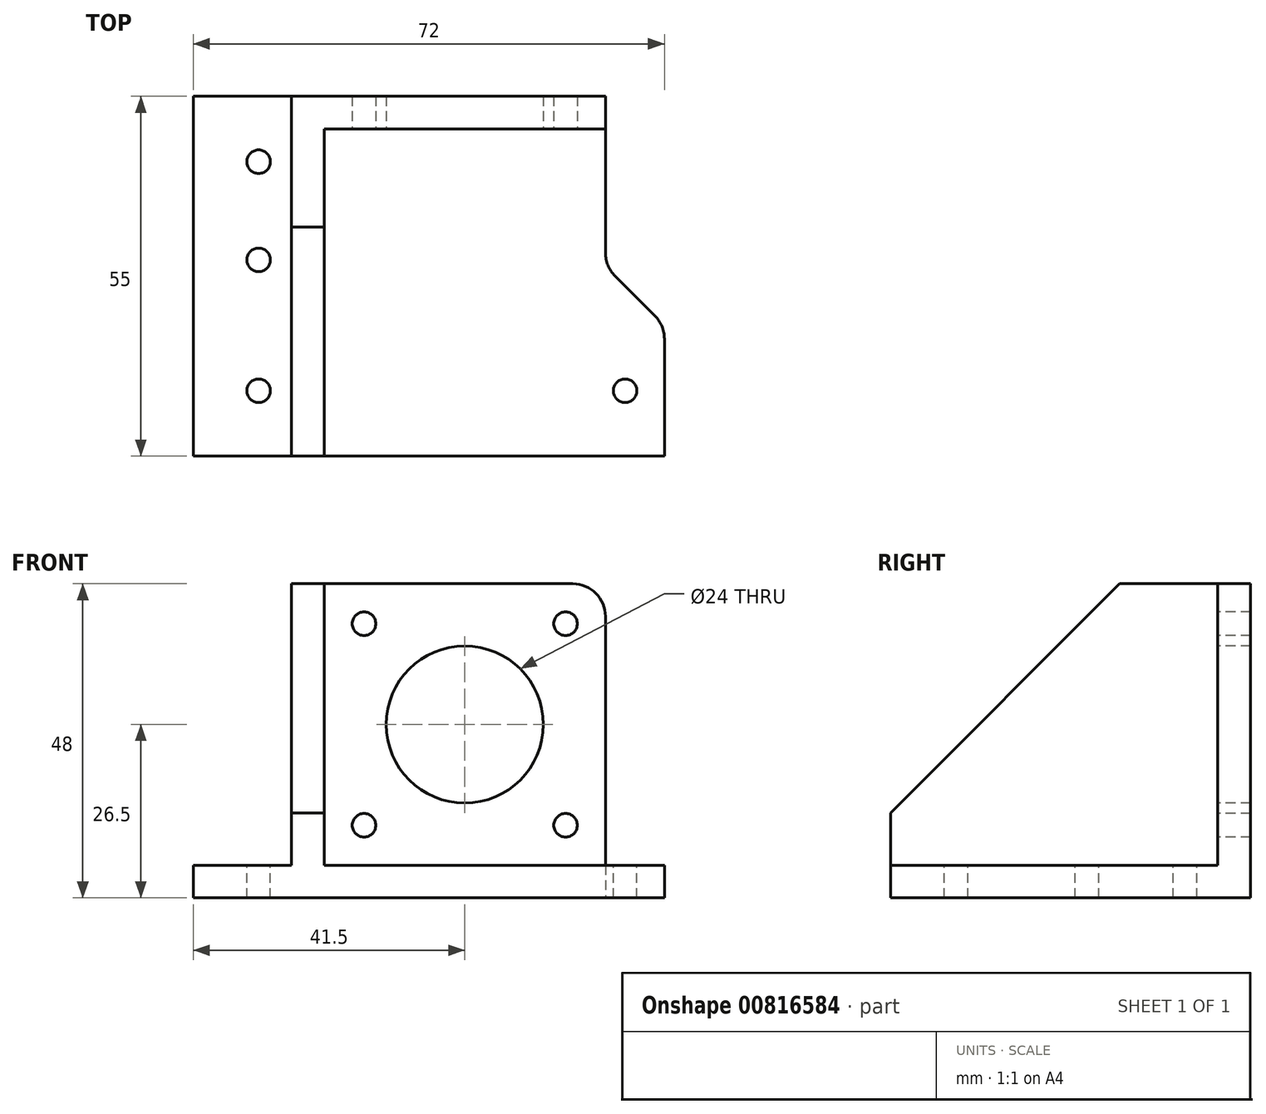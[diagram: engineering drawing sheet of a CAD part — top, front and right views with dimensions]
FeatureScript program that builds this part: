
annotation { "Feature Type Name" : "Feature", "Feature Type Description" : "" }
export const myFeature = defineFeature(function(context is Context, id is Id, definition is map)
    precondition{}
    {
        {
            var Q0;
            Q0=qCreatedBy(makeId("Top.planeOp"),FACE);
            var sketch = newSketch(context, id + "F0", { "sketchPlane" : qUnion([Q0])});
            skLineSegment(sketch, "E0.bottom", {"start": v(-36, -27.5) * mm, "end": v(36, -27.5) * mm});
            skLineSegment(sketch, "E0.top", {"start": v(-36, 27.5) * mm, "end": v(36, 27.5) * mm});
            skLineSegment(sketch, "E0.left", {"start": v(-36, -27.5) * mm, "end": v(-36, 27.5) * mm});
            skLineSegment(sketch, "E0.right", {"start": v(36, -27.5) * mm, "end": v(36, 27.5) * mm});
            skLineSegment(sketch, "E1", {"start": v(0, 27.5) * mm, "end": v(0, -27.5) * mm, "construction": true});
            skLineSegment(sketch, "E2", {"start": v(27, 27.5) * mm, "end": v(27, 1.5) * mm});
            skLineSegment(sketch, "E3", {"start": v(27, 1.5) * mm, "end": v(36, -7.5) * mm});
            skSolve(sketch);
        }
        {
            var Q0;
            {var subQ1=sQuery(id+"F0.wireOp",EDGE,"E0.bottom");Q0=makeQuery(id+"F0.imprint","IMPRINT",FACE,{"disambiguationData":[TD([[makeQuery(id+"F0.imprint","IMPRINT",EDGE,{"derivedFrom":subQ1}),1.0]])]});}
            extrude(context, id + "F1", {"entities" : qUnion([Q0]), "depth" : 5 * mm, "offsetDistance" : 25 * mm});
        }
        {
            var Q0;
            Q0=makeQuery(id+"F1.opExtrude","CAP_FACE",FACE,{"disambiguationData":[OSD([sQuery(id+"F0.wireOp",EDGE,"E0.bottom"),sQuery(id+"F0.wireOp",EDGE,"E0.top"),sQuery(id+"F0.wireOp",EDGE,"E0.left"),sQuery(id+"F0.wireOp",EDGE,"E0.right"),sQuery(id+"F0.wireOp",EDGE,"E2"),sQuery(id+"F0.wireOp",EDGE,"E3")])],"isStart":false});
            var sketch = newSketch(context, id + "F2", { "sketchPlane" : qUnion([Q0])});
            skLineSegment(sketch, "E4", {"start": v(-26, 27.5) * mm, "end": v(-26, -27.5) * mm, "construction": true});
            skCircle(sketch, "E5", {"center": v(-26, 2.5) * mm, "radius": 1.8 * mm});
            skCircle(sketch, "E6", {"center": v(-26, 17.5) * mm, "radius": 1.8 * mm});
            skCircle(sketch, "E7", {"center": v(-26, -17.5) * mm, "radius": 1.8 * mm});
            skLineSegment(sketch, "E8", {"start": v(36, -7.5) * mm, "end": v(-36, -7.5) * mm, "construction": true});
            skCircle(sketch, "E9", {"center": v(30, -17.5) * mm, "radius": 1.8 * mm});
            skSolve(sketch);
        }
        {
            var Q0;
            Q0=makeQuery(id+"F2.imprint","IMPRINT",FACE,{"disambiguationData":[TD([[makeQuery(id+"F2.imprint","IMPRINT",EDGE,{"derivedFrom":sQuery(id+"F2.wireOp",EDGE,"E6")}),1.0]])]});
            var Q1;
            Q1=makeQuery(id+"F2.imprint","IMPRINT",FACE,{"disambiguationData":[TD([[makeQuery(id+"F2.imprint","IMPRINT",EDGE,{"derivedFrom":sQuery(id+"F2.wireOp",EDGE,"E5")}),1.0]])]});
            var Q2;
            Q2=makeQuery(id+"F2.imprint","IMPRINT",FACE,{"disambiguationData":[TD([[makeQuery(id+"F2.imprint","IMPRINT",EDGE,{"derivedFrom":sQuery(id+"F2.wireOp",EDGE,"E7")}),1.0]])]});
            var Q3;
            Q3=makeQuery(id+"F2.imprint","IMPRINT",FACE,{"disambiguationData":[TD([[makeQuery(id+"F2.imprint","IMPRINT",EDGE,{"derivedFrom":sQuery(id+"F2.wireOp",EDGE,"E9")}),1.0]])]});
            extrude(context, id + "F3", {"entities" : qUnion([Q0, Q1, Q2, Q3]), "operationType" : NewBodyOperationType.REMOVE, "oppositeDirection" : true, "depth" : 25 * mm, "offsetDistance" : 25 * mm});
        }
        {
            var Q0;
            Q0=makeQuery(id+"F1.opExtrude","CAP_FACE",FACE,{"disambiguationData":[OSD([sQuery(id+"F0.wireOp",EDGE,"E0.bottom"),sQuery(id+"F0.wireOp",EDGE,"E0.top"),sQuery(id+"F0.wireOp",EDGE,"E0.left"),sQuery(id+"F0.wireOp",EDGE,"E0.right"),sQuery(id+"F0.wireOp",EDGE,"E2"),sQuery(id+"F0.wireOp",EDGE,"E3")])],"isStart":false});
            var sketch = newSketch(context, id + "F4", { "sketchPlane" : qUnion([Q0])});
            skLineSegment(sketch, "E10", {"start": v(-16, 27.5) * mm, "end": v(-16, -27.5) * mm, "construction": true});
            skLineSegment(sketch, "E11", {"start": v(27, 22.5) * mm, "end": v(-16, 22.5) * mm});
            skLineSegment(sketch, "E12", {"start": v(-16, 22.5) * mm, "end": v(-16, -27.5) * mm});
            skLineSegment(sketch, "E13", {"start": v(-21, 27.5) * mm, "end": v(-21, -27.5) * mm});
            skSolve(sketch);
        }
        {
            var Q0;
            {var subQ3=sQuery(id+"F4.wireOp",EDGE,"E11");Q0=makeQuery(id+"F4.imprint","IMPRINT",FACE,{"disambiguationData":[TD([[makeQuery(id+"F4.imprint","IMPRINT",EDGE,{"derivedFrom":subQ3}),-1.0]])]});}
            extrude(context, id + "F5", {"entities" : qUnion([Q0]), "operationType" : NewBodyOperationType.ADD, "depth" : 43 * mm, "offsetDistance" : 25 * mm});
        }
        {
            var Q0;
            Q0=makeQuery(id+"F5.opExtrude","SWEPT_FACE",FACE,{"disambiguationData":[OSD([sQuery(id+"F4.wireOp",EDGE,"E12")])]});
            var sketch = newSketch(context, id + "F6", { "sketchPlane" : qUnion([Q0])});
            skLineSegment(sketch, "E14", {"start": v(7.5, 48) * mm, "end": v(-27.5, 13) * mm});
            skSolve(sketch);
        }
        {
            var Q0;
            {var subQ0=sQuery(id+"F6.wireOp",EDGE,"E14");Q0=makeQuery(id+"F6.imprint","IMPRINT",FACE,{"disambiguationData":[TD([[makeQuery(id+"F6.imprint","IMPRINT",EDGE,{"derivedFrom":subQ0}),-1.0]])]});}
            extrude(context, id + "F7", {"entities" : qUnion([Q0]), "operationType" : NewBodyOperationType.REMOVE, "oppositeDirection" : true, "depth" : 25 * mm, "offsetDistance" : 25 * mm});
        }
        {
            var Q0;
            Q0=makeQuery(id+"F5.opExtrude","SWEPT_FACE",FACE,{"disambiguationData":[OSD([sQuery(id+"F4.wireOp",EDGE,"E11")])]});
            var sketch = newSketch(context, id + "F8", { "sketchPlane" : qUnion([Q0])});
            skLineSegment(sketch, "E15", {"start": v(5.5, 48) * mm, "end": v(5.5, 5) * mm, "construction": true});
            skCircle(sketch, "E16", {"center": v(5.5, 26.5) * mm, "radius": 12 * mm});
            skCircle(sketch, "E17", {"center": v(-9.9, 41.9) * mm, "radius": 1.8 * mm});
            skLineSegment(sketch, "E18", {"start": v(5.5, 26.5) * mm, "end": v(-9.9, 26.5) * mm, "construction": true});
            skCircle(sketch, "E19.0.1.0", {"center": v(-9.9, 11.1) * mm, "radius": 1.8 * mm});
            skCircle(sketch, "E19.1.0.0", {"center": v(20.9, 41.9) * mm, "radius": 1.8 * mm});
            skCircle(sketch, "E19.1.1.0", {"center": v(20.9, 11.1) * mm, "radius": 1.8 * mm});
            skLineSegment(sketch, "E19.direction1", {"start": v(-9.9, 41.9) * mm, "end": v(20.9, 41.9) * mm, "construction": true});
            skLineSegment(sketch, "E19.direction2", {"start": v(-9.9, 41.9) * mm, "end": v(-9.9, 11.1) * mm, "construction": true});
            skLineSegment(sketch, "E20", {"start": v(5.5, 5) * mm, "end": v(-16, 5) * mm, "construction": true});
            skSolve(sketch);
        }
        {
            var Q0;
            Q0=makeQuery(id+"F8.imprint","IMPRINT",FACE,{"disambiguationData":[TD([[makeQuery(id+"F8.imprint","IMPRINT",EDGE,{"derivedFrom":sQuery(id+"F8.wireOp",EDGE,"E16")}),1.0]])]});
            var Q1;
            Q1=makeQuery(id+"F8.imprint","IMPRINT",FACE,{"disambiguationData":[TD([[makeQuery(id+"F8.imprint","IMPRINT",EDGE,{"derivedFrom":sQuery(id+"F8.wireOp",EDGE,"E17")}),1.0]])]});
            var Q2;
            Q2=makeQuery(id+"F8.imprint","IMPRINT",FACE,{"disambiguationData":[TD([[makeQuery(id+"F8.imprint","IMPRINT",EDGE,{"derivedFrom":sQuery(id+"F8.wireOp",EDGE,"E19.0.1.0")}),1.0]])]});
            var Q3;
            Q3=makeQuery(id+"F8.imprint","IMPRINT",FACE,{"disambiguationData":[TD([[makeQuery(id+"F8.imprint","IMPRINT",EDGE,{"derivedFrom":sQuery(id+"F8.wireOp",EDGE,"E19.1.0.0")}),1.0]])]});
            var Q4;
            Q4=makeQuery(id+"F8.imprint","IMPRINT",FACE,{"disambiguationData":[TD([[makeQuery(id+"F8.imprint","IMPRINT",EDGE,{"derivedFrom":sQuery(id+"F8.wireOp",EDGE,"E19.1.1.0")}),1.0]])]});
            extrude(context, id + "F9", {"entities" : qUnion([Q0, Q1, Q2, Q3, Q4]), "operationType" : NewBodyOperationType.REMOVE, "oppositeDirection" : true, "depth" : 25 * mm, "offsetDistance" : 25 * mm});
        }
        {
            var Q0;
            Q0=makeQuery(id+"F7.boolean.opBoolean","COPY",EDGE,{"derivedFrom":makeQuery(id+"F7.opExtrude","SWEPT_EDGE",EDGE,{"disambiguationData":[OSD([sQuery(id+"F4.wireOp",EDGE,"E12"),sQuery(id+"F6.wireOp",EDGE,"E14")])]})});
            var Q1;
            Q1=makeQuery(id+"F7.boolean.opBoolean","COPY",EDGE,{"derivedFrom":makeQuery(id+"F7.opExtrude","SWEPT_EDGE",EDGE,{"disambiguationData":[OSD([sQuery(id+"F0.wireOp",EDGE,"E0.bottom"),sQuery(id+"F4.wireOp",EDGE,"E12"),sQuery(id+"F6.wireOp",EDGE,"E14")])]})});
            var Q2;
            Q2=makeQuery(id+"F5.opExtrude","CAP_EDGE",EDGE,{"disambiguationData":[OSD([sQuery(id+"F0.wireOp",EDGE,"E2")])],"isStart":false});
            var Q3;
            Q3=makeQuery(id+"F1.opExtrude","SWEPT_EDGE",EDGE,{"disambiguationData":[OSD([sQuery(id+"F0.wireOp",EDGE,"E0.right"),sQuery(id+"F0.wireOp",EDGE,"E3")])]});
            var Q4;
            Q4=makeQuery(id+"F1.opExtrude","SWEPT_EDGE",EDGE,{"disambiguationData":[OSD([sQuery(id+"F0.wireOp",EDGE,"E2"),sQuery(id+"F0.wireOp",EDGE,"E3")])]});
            fillet(context, id + "F10", {"entities" : qUnion([Q0, Q1, Q2, Q3, Q4]), "radius" : 5 * mm, "tangentPropagation" : true, "allowEdgeOverflow" : false});
        }
    });
